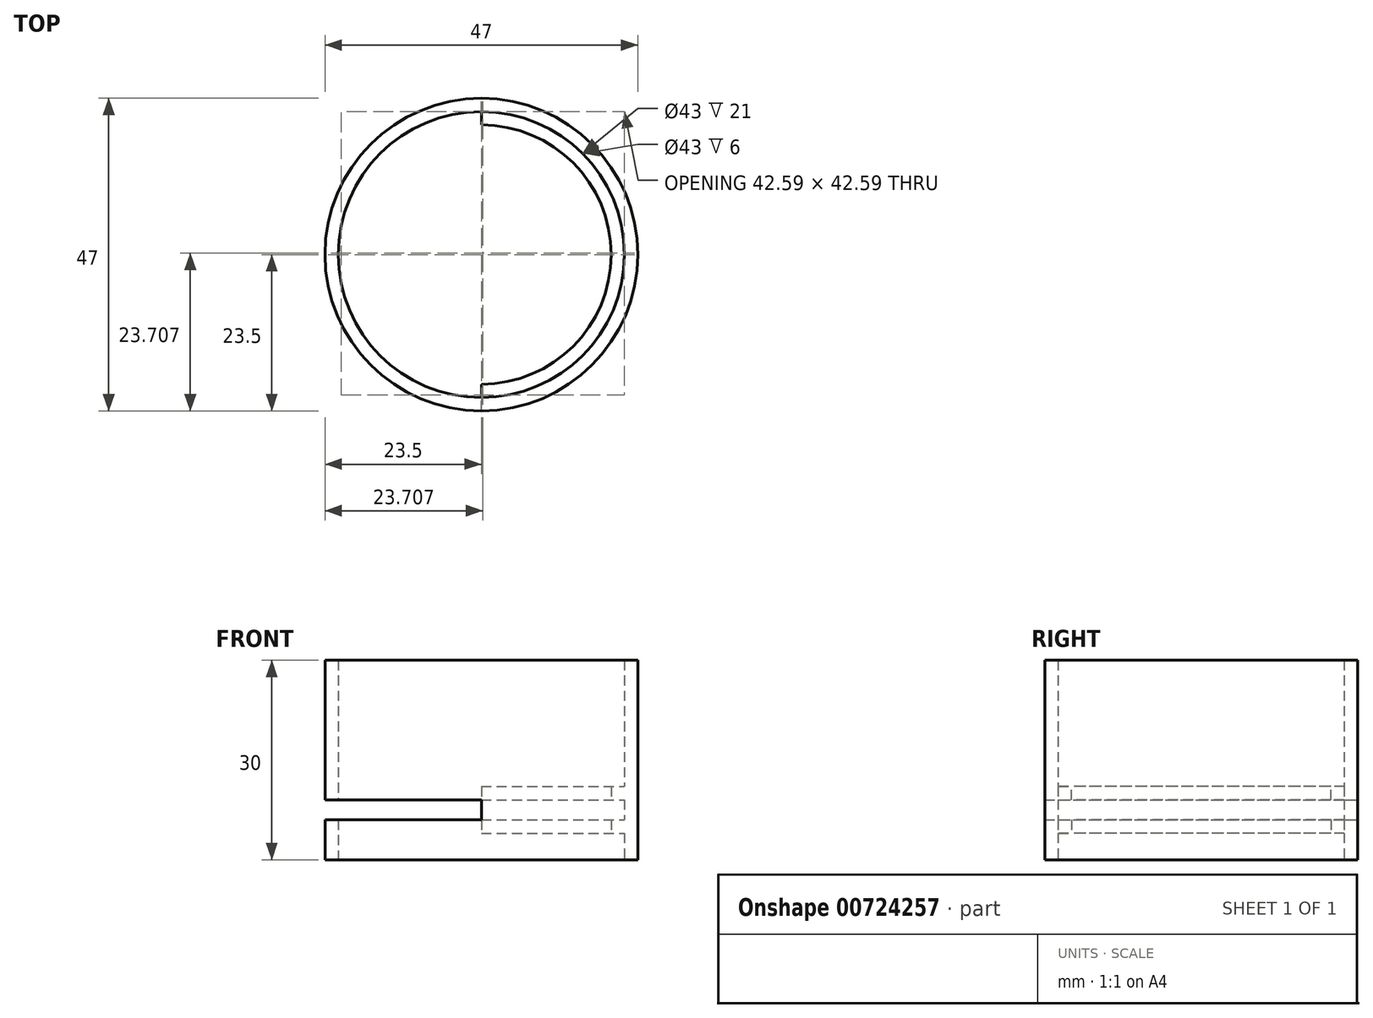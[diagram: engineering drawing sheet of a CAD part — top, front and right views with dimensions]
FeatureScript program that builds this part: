
annotation { "Feature Type Name" : "Feature", "Feature Type Description" : "" }
export const myFeature = defineFeature(function(context is Context, id is Id, definition is map)
    precondition{}
    {
        {
            var Q0;
            Q0=qCreatedBy(makeId("Top.planeOp"),FACE);
            var sketch = newSketch(context, id + "F0", { "sketchPlane" : qUnion([Q0])});
            skCircle(sketch, "E0", {"center": v(0, 0) * mm, "radius": 23.5 * mm});
            skCircle(sketch, "E1", {"center": v(0, 0) * mm, "radius": 21.5 * mm});
            skSolve(sketch);
        }
        {
            var Q0;
            Q0=makeQuery(id+"F0.imprint","IMPRINT",FACE,{"disambiguationData":[TD([[makeQuery(id+"F0.imprint","IMPRINT",EDGE,{"derivedFrom":sQuery(id+"F0.wireOp",EDGE,"E0")}),1.0]])]});
            extrude(context, id + "F1", {"entities" : qUnion([Q0]), "depth" : 30 * mm, "offsetDistance" : 25 * mm});
        }
        {
            var Q0;
            Q0=qCreatedBy(makeId("Right.planeOp"),FACE);
            var sketch = newSketch(context, id + "F2", { "sketchPlane" : qUnion([Q0])});
            skLineSegment(sketch, "E2", {"start": v(-23.5, 0) * mm, "end": v(-23.5, 15) * mm});
            skLineSegment(sketch, "E3", {"start": v(23.5, 15) * mm, "end": v(23.5, 0) * mm});
            skLineSegment(sketch, "E4.0", {"start": v(-23.5, 30) * mm, "end": v(23.5, 30) * mm});
            skLineSegment(sketch, "E5", {"start": v(-23.5, 7.5) * mm, "end": v(23.5, 7.5) * mm, "construction": true});
            skLineSegment(sketch, "E6", {"start": v(0, 30) * mm, "end": v(0, 0) * mm, "construction": true});
            skLineSegment(sketch, "E7.bottom", {"start": v(-23.5, 9) * mm, "end": v(23.5, 9) * mm});
            skLineSegment(sketch, "E7.top", {"start": v(-23.5, 6) * mm, "end": v(23.5, 6) * mm});
            skLineSegment(sketch, "E7.left", {"start": v(-23.5, 9) * mm, "end": v(-23.5, 6) * mm});
            skLineSegment(sketch, "E7.right", {"start": v(23.5, 9) * mm, "end": v(23.5, 6) * mm});
            skLineSegment(sketch, "E8", {"start": v(-11.59, 9) * mm, "end": v(-11.59, 7.5) * mm, "construction": true});
            skLineSegment(sketch, "E9", {"start": v(-8.87, 7.5) * mm, "end": v(-8.87, 6) * mm, "construction": true});
            skSolve(sketch);
        }
        {
            var Q0;
            Q0=makeQuery(id+"F2.imprint","IMPRINT",FACE,{"disambiguationData":[TD([[makeQuery(id+"F2.imprint","IMPRINT",EDGE,{"derivedFrom":sQuery(id+"F2.wireOp",EDGE,"E7.bottom")}),-1.0]])]});
            extrude(context, id + "F3", {"entities" : qUnion([Q0]), "operationType" : NewBodyOperationType.REMOVE, "endBound" : BoundingType.THROUGH_ALL, "oppositeDirection" : true, "depth" : 25 * mm, "offsetDistance" : 25 * mm});
        }
        {
            var Q0;
            Q0=qCreatedBy(makeId("Front.planeOp"),FACE);
            var sketch = newSketch(context, id + "F4", { "sketchPlane" : qUnion([Q0])});
            skLineSegment(sketch, "E10", {"start": v(-21.5, 0) * mm, "end": v(-21.5, 30) * mm});
            skLineSegment(sketch, "E11", {"start": v(21.5, 30) * mm, "end": v(21.5, 0) * mm});
            skLineSegment(sketch, "E12.0", {"start": v(0, 6) * mm, "end": v(0, 9) * mm});
            skLineSegment(sketch, "E13", {"start": v(0, -26.09) * mm, "end": v(0, 44.1) * mm, "construction": true});
            skLineSegment(sketch, "E14.bottom", {"start": v(21.5, 9) * mm, "end": v(19.5, 9) * mm});
            skLineSegment(sketch, "E14.top", {"start": v(21.5, 11) * mm, "end": v(19.5, 11) * mm});
            skLineSegment(sketch, "E14.left", {"start": v(21.5, 9) * mm, "end": v(21.5, 11) * mm});
            skLineSegment(sketch, "E14.right", {"start": v(19.5, 9) * mm, "end": v(19.5, 11) * mm});
            skLineSegment(sketch, "E15.bottom", {"start": v(21.5, 6) * mm, "end": v(19.5, 6) * mm});
            skLineSegment(sketch, "E15.top", {"start": v(21.5, 4) * mm, "end": v(19.5, 4) * mm});
            skLineSegment(sketch, "E15.left", {"start": v(21.5, 6) * mm, "end": v(21.5, 4) * mm});
            skLineSegment(sketch, "E15.right", {"start": v(19.5, 6) * mm, "end": v(19.5, 4) * mm});
            skSolve(sketch);
        }
        {
            var Q0;
            Q0=makeQuery(id+"F4.imprint","IMPRINT",FACE,{"disambiguationData":[TD([[makeQuery(id+"F4.imprint","IMPRINT",EDGE,{"derivedFrom":sQuery(id+"F4.wireOp",EDGE,"E14.bottom")}),-1.0]])]});
            var Q1;
            Q1=makeQuery(id+"F4.imprint","IMPRINT",FACE,{"disambiguationData":[TD([[makeQuery(id+"F4.imprint","IMPRINT",EDGE,{"derivedFrom":sQuery(id+"F4.wireOp",EDGE,"E15.bottom")}),1.0]])]});
            var Q2;
            Q2=sQuery(id+"F4.wireOp",EDGE,"E13");
            revolve(context, id + "F5", {"operationType" : NewBodyOperationType.ADD, "surfaceOperationType" : NewSurfaceOperationType.NEW, "entities" : qUnion([Q0, Q1]), "axis" : qUnion([Q2]), "revolveType" : RevolveType.SYMMETRIC, "angle" : 180 * degree});
        }
    });
